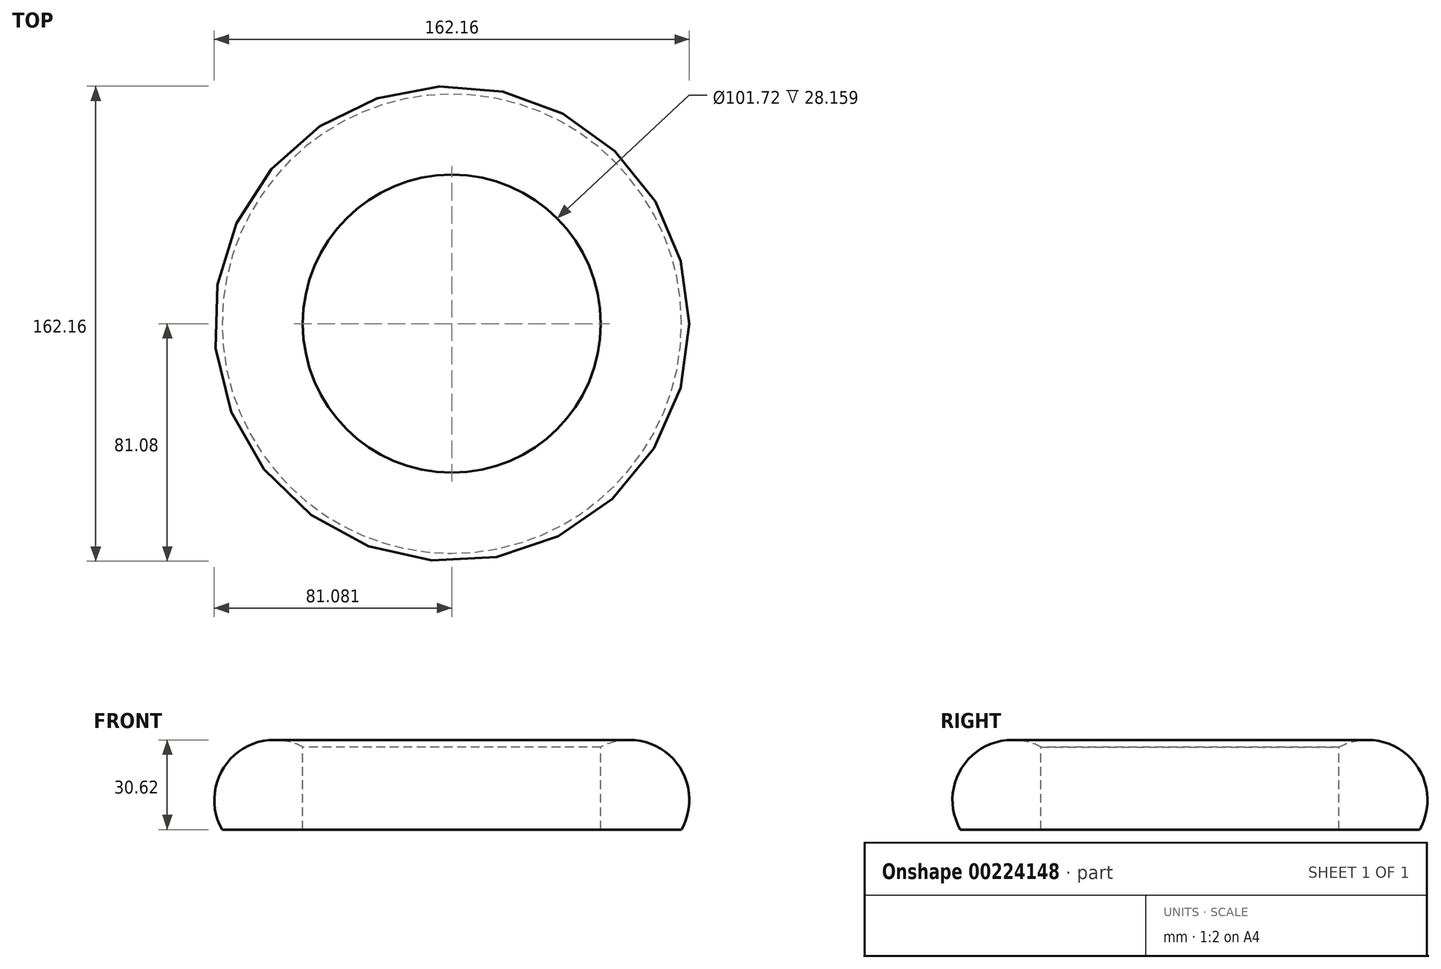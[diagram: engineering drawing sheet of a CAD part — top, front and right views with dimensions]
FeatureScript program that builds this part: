
annotation { "Feature Type Name" : "Feature", "Feature Type Description" : "" }
export const myFeature = defineFeature(function(context is Context, id is Id, definition is map)
    precondition{}
    {
        {
            var Q0;
            Q0=qCreatedBy(makeId("Front.planeOp"),FACE);
            var sketch = newSketch(context, id + "F0", { "sketchPlane" : qUnion([Q0])});
            skLineSegment(sketch, "E0", {"start": v(0, 28.16) * mm, "end": v(0, 0) * mm});
            skLineSegment(sketch, "E1", {"start": v(0, 0) * mm, "end": v(27.54, 0) * mm});
            skArc(sketch, "E2", {"start": v(27.54, 0) * mm, "mid": v(24.38, 24.46) * mm, "end": v(0, 28.16) * mm});
            skLineSegment(sketch, "E3", {"start": v(-50.86, 28.65) * mm, "end": v(-50.86, -46.52) * mm});
            skSolve(sketch);
        }
        {
            var Q0;
            Q0=makeQuery(id+"F0.imprint","IMPRINT",FACE,{"disambiguationData":[TD([[makeQuery(id+"F0.imprint","IMPRINT",EDGE,{"derivedFrom":sQuery(id+"F0.wireOp",EDGE,"E0")}),1.0]])]});
            var Q1;
            Q1=sQuery(id+"F0.wireOp",EDGE,"E3");
            revolve(context, id + "F1", {"entities" : qUnion([Q0]), "axis" : qUnion([Q1]), "revolveType" : RevolveType.FULL});
        }
    });
